# Revit family: KEUCO_14910010000
name_source: partatom
category: Allgemeines Modell
revit_build: Autodesk Revit 2016 (Build: 20150220_1215(x64)
units: mm (PartAtom-declared; Revit-internal decimal feet)

## family parameters
Arbeitsebenenbasiert = Ja
Beim Laden mit Abzugskörper schneiden = Nein
Bemaßung runder Anschluss = Durchmesser verwenden
Gemeinsam genutzt = Nein
Immer vertikal = Nein
Kann Basisbauteil für Bewehrung sein = Nein
Raumberechnungspunkt = Nein
Teiletyp = Normal

## types (3) — shared parameters
Beschreibung = ohne Platte
Gewicht = 0.522
Hersteller = KEUCO
Kategorie = ACC
Material Regal = Glas, weiß, hohe Luminanz
Regal Länge = 220 mm  [stored 0.721785 ft]
Serie = Plan
Tiefe = 100 mm  [stored 0.328084 ft]
URL = https://www.keuco.com
Verwendung = GWC / WP
Vorgabe-Ansicht = 1219 mm

## per-type parameters (varying)
| type | Ausschreibungstext | Rahmen Material | Regal Länge Variation |
| 14910010000 | KEUCO PLAN Ablagekonsole 14910010000 
Hochglanzverchromte Ablagekonsole 
in ästhetischem, funktionalem Design 
passend zu der Glasplatte Artikel-Nr. 14910 und 14958 
Breite 210 mm, Höhe 22 mm 
Die Ablagekonsole wird verdeckt angebracht
Lieferung inkl. korrosionsfreiem Befestigungsmaterial
Die Glasplatte ist separat zu bestellen! | Verchromt | 1 |
| 14910070000 | KEUCO PLAN Ablagekonsole 14910070000 
Zeitlose Ablagekonsole aus hochwertigem Edelstahl
in ästhetischem, funktionalem Design 
passend zu der Glasplatte Artikel-Nr. 14910 und 14958
Breite 210 mm, Höhe 22 mm 
Die Ablagekonsole wird verdeckt angebracht
Lieferung inkl. korrosionsfreiem Befestigungsmaterial
Die Glasplatte ist separat zu bestellen! | Aluminium silber-eloxiert (E6 EV1) | 0 |
| 14910170000 | KEUCO PLAN Ablagekonsole 14910170000
Ablagekonsole aus 
hochwertigem silber-eloxiertem Aluminium (E6 EV1)/verchromt 
in ästhetischem, funktionalem Design 
passend zu der Glasplatte Artikel-Nr. 14910 und 14958
Die Wandhalterung ist als Design-Element hochglanzverchromt 
Breite 210 mm, Höhe 22 mm 
De Ablagekonsole wird verdeckt angebracht 
Lieferung inkl. korrosionsfreiem Befestigungsmaterial
Die Glasplatte ist separat zu bestellen! | Aluminium silber-eloxiert (E6 EV1) | 1 |

note: column(s) folded — value = type name in every type: Artikelnummer

note: [stored X ft] marks values corroborated as IEEE doubles in the binary element streams (Revit-internal decimal feet)

## geometry (parser evidence)
native form markers: Blend x2, Sweep x3
no freeform markers — native parametric forms only
